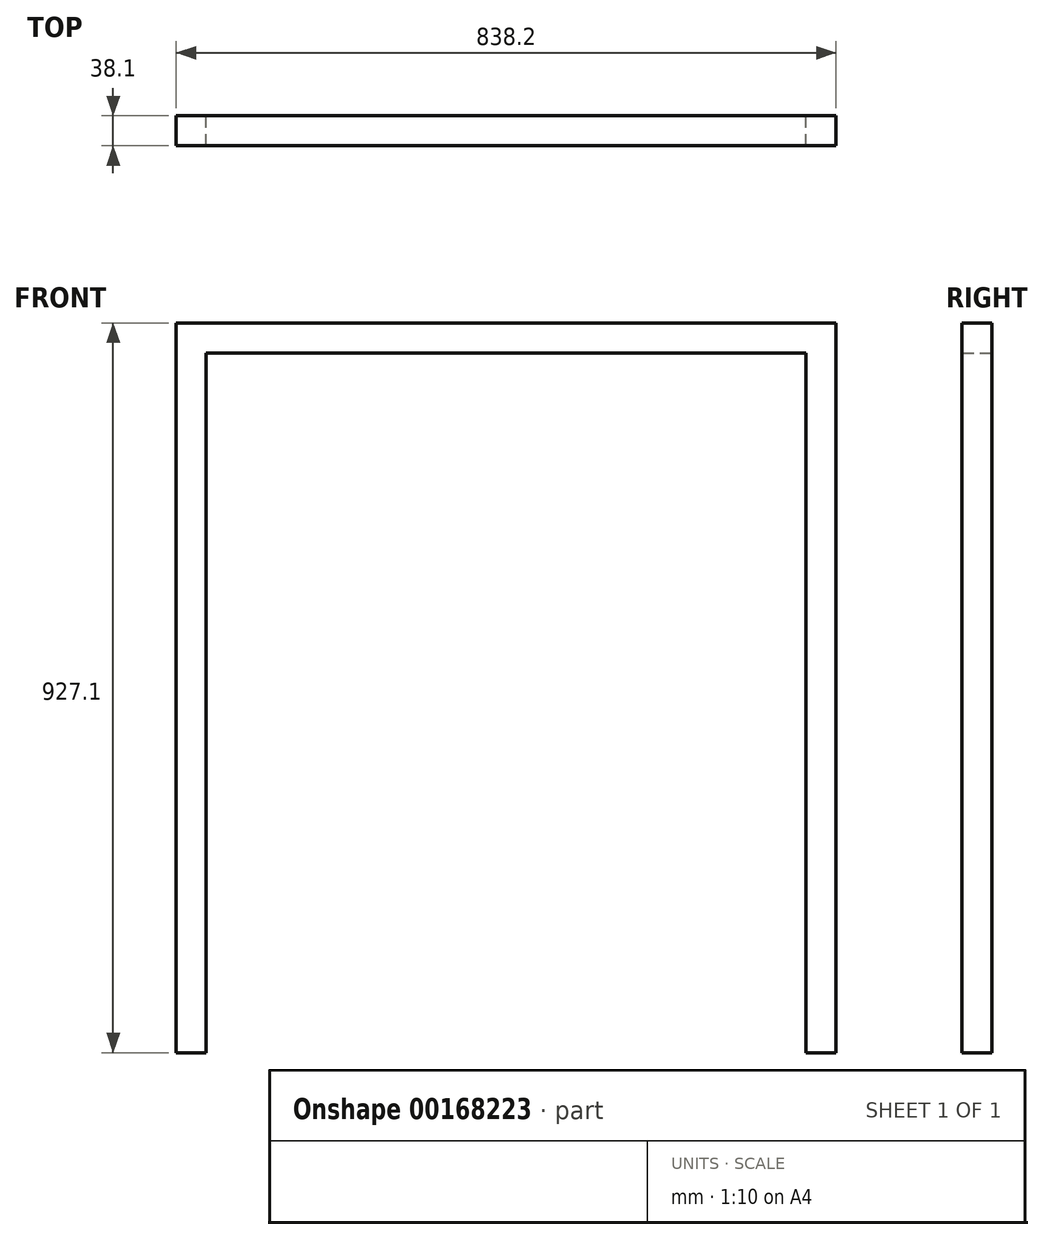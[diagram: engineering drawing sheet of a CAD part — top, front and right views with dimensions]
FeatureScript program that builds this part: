
annotation { "Feature Type Name" : "Feature", "Feature Type Description" : "" }
export const myFeature = defineFeature(function(context is Context, id is Id, definition is map)
    precondition{}
    {
        {
            var Q0;
            Q0=qCreatedBy(makeId("Front.planeOp"),FACE);
            var sketch = newSketch(context, id + "F0", { "sketchPlane" : qUnion([Q0])});
            skLineSegment(sketch, "E0", {"start": v(-418.18, 0) * mm, "end": v(-418.18, 927.1) * mm});
            skLineSegment(sketch, "E1", {"start": v(-418.18, 927.1) * mm, "end": v(420.02, 927.1) * mm});
            skLineSegment(sketch, "E2", {"start": v(420.02, 927.1) * mm, "end": v(420.02, 0) * mm});
            skLineSegment(sketch, "E3", {"start": v(-418.18, 0) * mm, "end": v(-380.08, 0) * mm});
            skLineSegment(sketch, "E4", {"start": v(420.02, 0) * mm, "end": v(381.92, 0) * mm});
            skLineSegment(sketch, "E5", {"start": v(-380.08, 0) * mm, "end": v(-380.08, 889) * mm});
            skLineSegment(sketch, "E6", {"start": v(-380.08, 889) * mm, "end": v(381.92, 889) * mm});
            skLineSegment(sketch, "E7", {"start": v(381.92, 889) * mm, "end": v(381.92, 0) * mm});
            skSolve(sketch);
        }
        {
            var Q0;
            Q0=makeQuery(id+"F0.imprint","IMPRINT",FACE,{"disambiguationData":[TD([[makeQuery(id+"F0.imprint","IMPRINT",EDGE,{"derivedFrom":sQuery(id+"F0.wireOp",EDGE,"E0")}),-1.0]])]});
            extrude(context, id + "F1", {"entities" : qUnion([Q0]), "depth" : 38.1 * mm});
        }
    });
